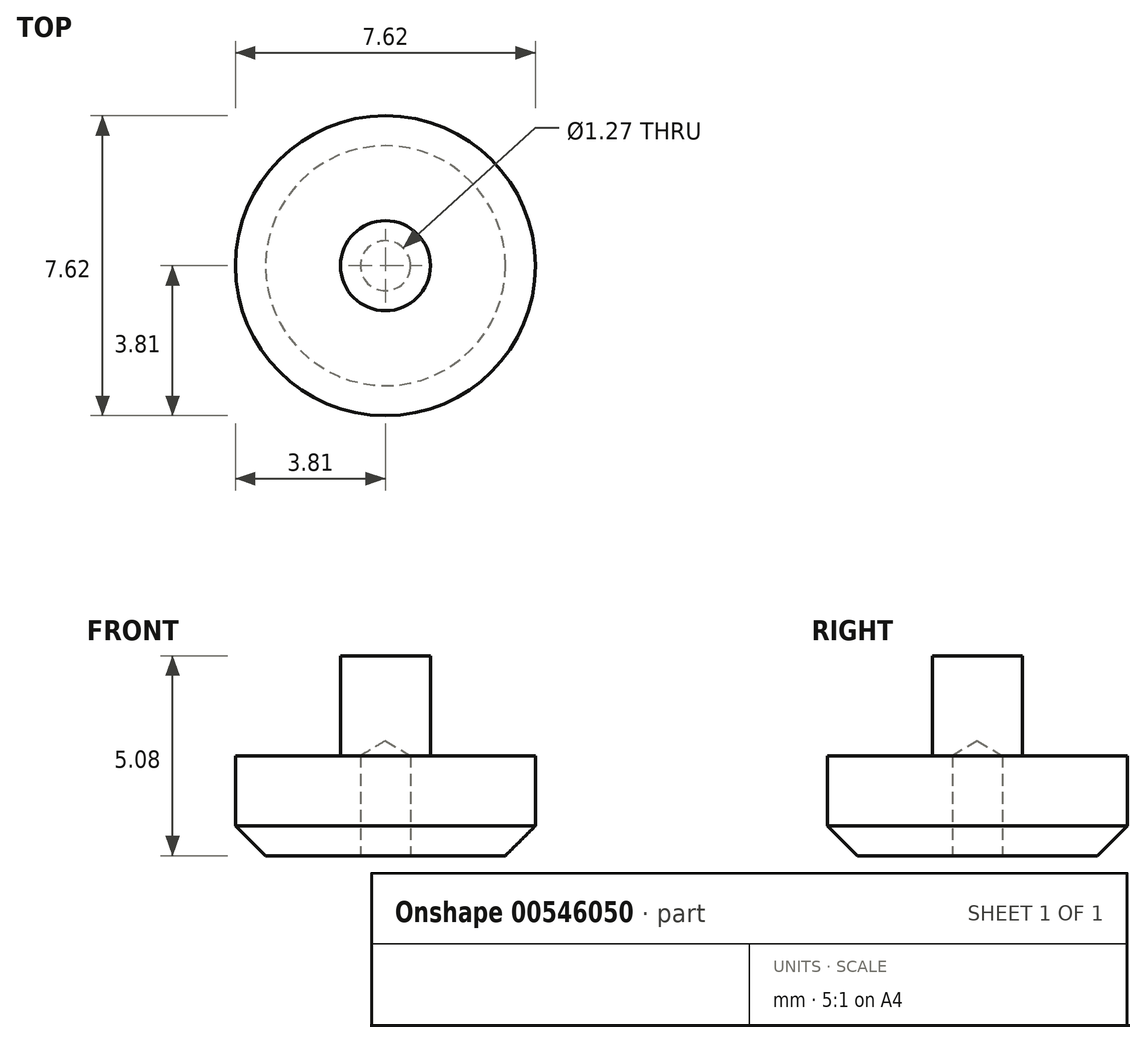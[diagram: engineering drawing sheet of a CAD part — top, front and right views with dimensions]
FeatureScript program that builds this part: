
annotation { "Feature Type Name" : "Feature", "Feature Type Description" : "" }
export const myFeature = defineFeature(function(context is Context, id is Id, definition is map)
    precondition{}
    {
        {
            var Q0;
            Q0=qCreatedBy(makeId("Top.planeOp"),FACE);
            var sketch = newSketch(context, id + "F0", { "sketchPlane" : qUnion([Q0])});
            skCircle(sketch, "E0", {"center": v(0, 0) * mm, "radius": 3.8 * mm});
            skSolve(sketch);
        }
        {
            var Q0;
            Q0 = qSketchRegion(id + "F0", true);
            extrude(context, id + "F1", {"entities" : qUnion([Q0]), "depth" : 2.54 * mm, "offsetDistance" : 25.4 * mm});
        }
        {
            var Q0;
            Q0=makeQuery(id+"F1.opExtrude","CAP_FACE",FACE,{"disambiguationData":[OSD([sQuery(id+"F0.wireOp",EDGE,"E0")])],"isStart":false});
            var sketch = newSketch(context, id + "F2", { "sketchPlane" : qUnion([Q0])});
            skCircle(sketch, "E1", {"center": v(0, 0) * mm, "radius": 1.14 * mm});
            skSolve(sketch);
        }
        {
            var Q0;
            Q0 = qSketchRegion(id + "F2", true);
            extrude(context, id + "F3", {"entities" : qUnion([Q0]), "operationType" : NewBodyOperationType.ADD, "depth" : 2.54 * mm, "offsetDistance" : 25.4 * mm});
        }
        {
            var Q0;
            Q0=makeQuery(id+"F1.opExtrude","CAP_FACE",FACE,{"disambiguationData":[OSD([sQuery(id+"F0.wireOp",EDGE,"E0")])],"isStart":true});
            var sketch = newSketch(context, id + "F4", { "sketchPlane" : qUnion([Q0])});
            skPoint(sketch, "E2", {"position": v(0, 0) * mm});
            skSolve(sketch);
        }
        {
            var Q0;
            Q0=sQuery(id+"F4.wireOp",VERTEX,"E2");
            var Q1;
            Q1=makeQuery(id+"F1.opExtrude","SWEPT_BODY",BODY,{"disambiguationData":[OSD([sQuery(id+"F0.wireOp",EDGE,"E0")])]});
            hole(context, id + "F5", {"style" : HoleStyle.SIMPLE, "endStyle" : HoleEndStyle.BLIND, "holeDiameter" : 1.27 * mm, "holeDepth" : 2.54 * mm, "isTappedThrough" : true, "tappedDepth" : 12.7 * mm, "tapClearance" : 3, "locations" : qUnion([Q0]), "scope" : qUnion([Q1])});
        }
        {
            var Q0;
            Q0=makeQuery(id+"F1.opExtrude","CAP_EDGE",EDGE,{"disambiguationData":[OSD([sQuery(id+"F0.wireOp",EDGE,"E0")])],"isStart":true});
            chamfer(context, id + "F6", {"entities" : qUnion([Q0]), "width" : 0.76 * mm, "tangentPropagation" : true});
        }
    });
